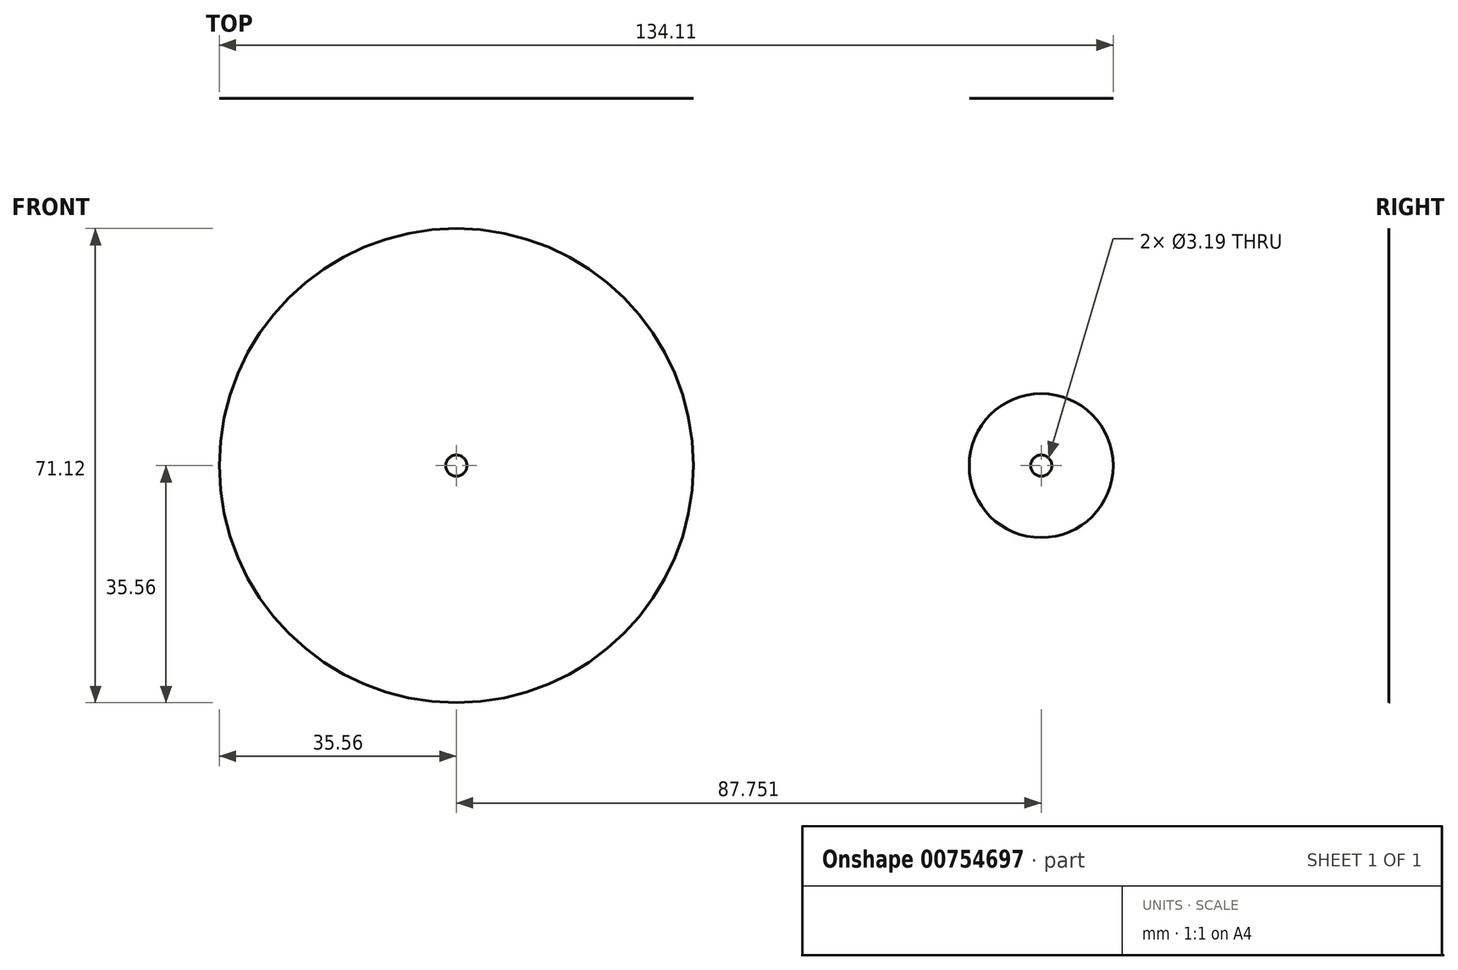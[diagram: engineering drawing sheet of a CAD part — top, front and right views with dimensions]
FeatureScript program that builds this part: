
annotation { "Feature Type Name" : "Feature", "Feature Type Description" : "" }
export const myFeature = defineFeature(function(context is Context, id is Id, definition is map)
    precondition{}
    {
        {
            var Q0;
            Q0=qCreatedBy(makeId("Front.planeOp"),FACE);
            var sketch = newSketch(context, id + "F0", { "sketchPlane" : qUnion([Q0])});
            skCircle(sketch, "E0", {"center": v(-53.33, 0) * mm, "radius": 35.56 * mm});
            skCircle(sketch, "E1", {"center": v(34.42, 0) * mm, "radius": 10.8 * mm});
            skCircle(sketch, "E2", {"center": v(-53.33, 0) * mm, "radius": 1.6 * mm});
            skCircle(sketch, "E3", {"center": v(34.42, 0) * mm, "radius": 1.6 * mm});
            skSolve(sketch);
        }
        {
            var Q0;
            Q0=makeQuery(id+"F0.imprint","IMPRINT",FACE,{"disambiguationData":[TD([[makeQuery(id+"F0.imprint","IMPRINT",EDGE,{"derivedFrom":sQuery(id+"F0.wireOp",EDGE,"E0")}),1.0]])]});
            var Q1;
            Q1=makeQuery(id+"F0.imprint","IMPRINT",FACE,{"disambiguationData":[TD([[makeQuery(id+"F0.imprint","IMPRINT",EDGE,{"derivedFrom":sQuery(id+"F0.wireOp",EDGE,"E1")}),1.0]])]});
            extrude(context, id + "F1", {"entities" : qUnion([Q0, Q1]), "endBound" : BoundingType.SYMMETRIC, "depth" : 1 / 203.2 * mm, "offsetDistance" : 25.4 * mm});
        }
    });
